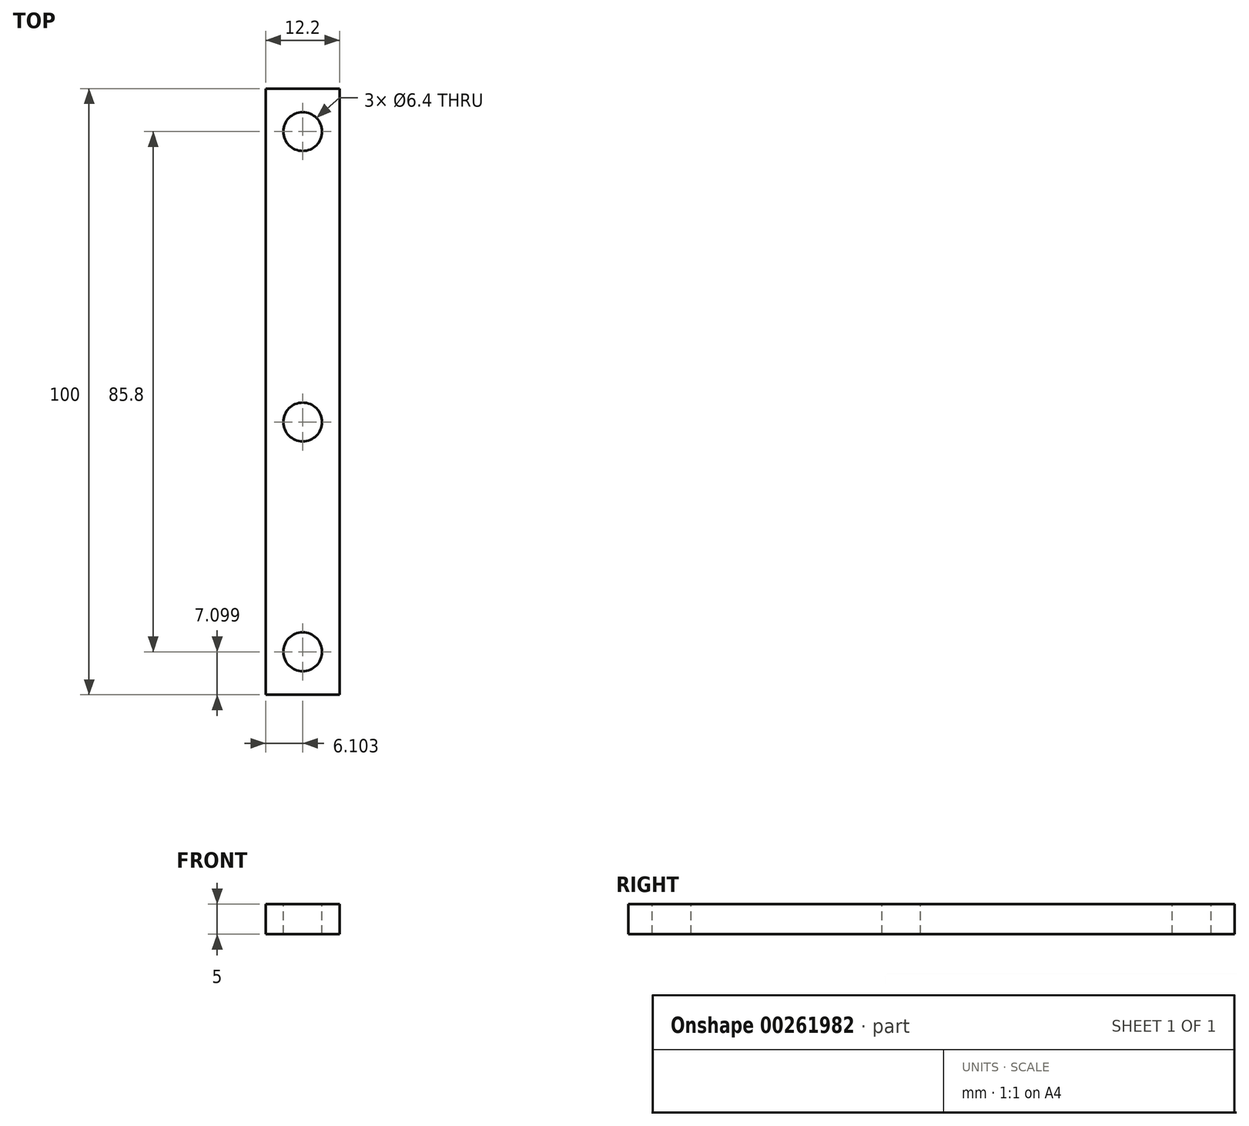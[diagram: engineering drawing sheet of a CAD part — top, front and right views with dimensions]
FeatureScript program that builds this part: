
annotation { "Feature Type Name" : "Feature", "Feature Type Description" : "" }
export const myFeature = defineFeature(function(context is Context, id is Id, definition is map)
    precondition{}
    {
        {
            var Q0;
            Q0=qCreatedBy(makeId("Top.planeOp"),FACE);
            var sketch = newSketch(context, id + "F0", { "sketchPlane" : qUnion([Q0])});
            skLineSegment(sketch, "E0.bottom", {"start": v(16.6, 47.89) * mm, "end": v(28.8, 47.89) * mm});
            skLineSegment(sketch, "E0.top", {"start": v(16.6, -52.11) * mm, "end": v(28.8, -52.11) * mm});
            skLineSegment(sketch, "E0.left", {"start": v(16.6, 47.89) * mm, "end": v(16.6, -52.11) * mm});
            skLineSegment(sketch, "E0.right", {"start": v(28.8, 47.89) * mm, "end": v(28.8, -52.11) * mm});
            skSolve(sketch);
        }
        {
            var Q0;
            Q0 = qSketchRegion(id + "F0", true);
            extrude(context, id + "F1", {"entities" : qUnion([Q0]), "depth" : 5 * mm});
        }
        {
            var Q0;
            Q0=makeQuery(id+"F1.opExtrude","CAP_FACE",FACE,{"disambiguationData":[OSD([sQuery(id+"F0.wireOp",EDGE,"E0.bottom"),sQuery(id+"F0.wireOp",EDGE,"E0.top"),sQuery(id+"F0.wireOp",EDGE,"E0.left"),sQuery(id+"F0.wireOp",EDGE,"E0.right")])],"isStart":false});
            var sketch = newSketch(context, id + "F2", { "sketchPlane" : qUnion([Q0])});
            skLineSegment(sketch, "E1", {"start": v(22.7, 47.89) * mm, "end": v(22.7, -52.11) * mm, "construction": true});
            skLineSegment(sketch, "E2.bottom", {"start": v(28.8, 47.89) * mm, "end": v(16.6, 47.89) * mm, "construction": true});
            skLineSegment(sketch, "E2.top", {"start": v(28.8, 40.79) * mm, "end": v(16.6, 40.79) * mm, "construction": true});
            skLineSegment(sketch, "E2.left", {"start": v(28.8, 47.89) * mm, "end": v(28.8, 40.79) * mm, "construction": true});
            skLineSegment(sketch, "E2.right", {"start": v(16.6, 47.89) * mm, "end": v(16.6, 40.79) * mm, "construction": true});
            skLineSegment(sketch, "E3.bottom", {"start": v(28.8, -52.11) * mm, "end": v(16.6, -52.11) * mm, "construction": true});
            skLineSegment(sketch, "E3.top", {"start": v(28.8, -45.01) * mm, "end": v(16.6, -45.01) * mm, "construction": true});
            skLineSegment(sketch, "E3.left", {"start": v(28.8, -52.11) * mm, "end": v(28.8, -45.01) * mm, "construction": true});
            skLineSegment(sketch, "E3.right", {"start": v(16.6, -52.11) * mm, "end": v(16.6, -45.01) * mm, "construction": true});
            skLineSegment(sketch, "E4.top", {"start": v(28.8, -7.11) * mm, "end": v(16.6, -7.11) * mm, "construction": true});
            skLineSegment(sketch, "E4.left", {"start": v(28.8, -52.11) * mm, "end": v(28.8, -7.11) * mm, "construction": true});
            skLineSegment(sketch, "E4.right", {"start": v(16.6, -52.11) * mm, "end": v(16.6, -7.11) * mm, "construction": true});
            skCircle(sketch, "E5", {"center": v(22.7, -45.01) * mm, "radius": 3.2 * mm});
            skCircle(sketch, "E6", {"center": v(22.7, -7.11) * mm, "radius": 3.2 * mm});
            skCircle(sketch, "E7", {"center": v(22.7, 40.79) * mm, "radius": 3.2 * mm});
            skSolve(sketch);
        }
        {
            var Q0;
            Q0=makeQuery(id+"F2.imprint","IMPRINT",FACE,{"disambiguationData":[TD([[makeQuery(id+"F2.imprint","IMPRINT",EDGE,{"derivedFrom":sQuery(id+"F2.wireOp",EDGE,"E5")}),1.0]])]});
            var Q1;
            Q1=makeQuery(id+"F2.imprint","IMPRINT",FACE,{"disambiguationData":[TD([[makeQuery(id+"F2.imprint","IMPRINT",EDGE,{"derivedFrom":sQuery(id+"F2.wireOp",EDGE,"E6")}),1.0]])]});
            var Q2;
            Q2=makeQuery(id+"F2.imprint","IMPRINT",FACE,{"disambiguationData":[TD([[makeQuery(id+"F2.imprint","IMPRINT",EDGE,{"derivedFrom":sQuery(id+"F2.wireOp",EDGE,"E7")}),1.0]])]});
            extrude(context, id + "F3", {"entities" : qUnion([Q0, Q1, Q2]), "operationType" : NewBodyOperationType.REMOVE, "oppositeDirection" : true, "depth" : 6 * mm});
        }
    });
